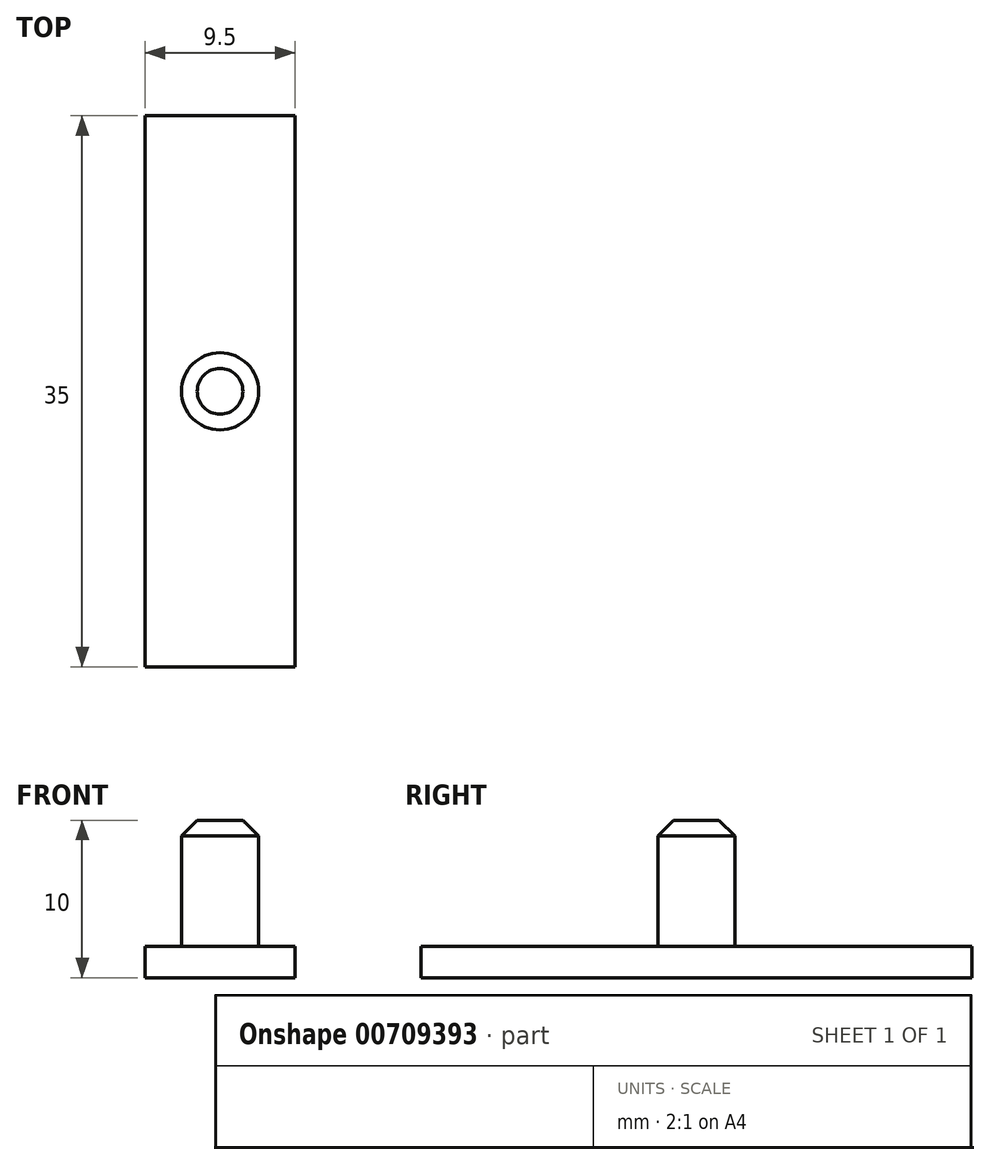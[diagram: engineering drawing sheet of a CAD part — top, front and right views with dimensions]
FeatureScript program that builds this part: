
annotation { "Feature Type Name" : "Feature", "Feature Type Description" : "" }
export const myFeature = defineFeature(function(context is Context, id is Id, definition is map)
    precondition{}
    {
        {
            var Q0;
            Q0=qCreatedBy(makeId("Top.planeOp"),FACE);
            var sketch = newSketch(context, id + "F0", { "sketchPlane" : qUnion([Q0])});
            skLineSegment(sketch, "E0.bottom", {"start": v(0, 0) * mm, "end": v(9.5, 0) * mm});
            skLineSegment(sketch, "E0.top", {"start": v(0, 35) * mm, "end": v(9.5, 35) * mm});
            skLineSegment(sketch, "E0.left", {"start": v(0, 0) * mm, "end": v(0, 35) * mm});
            skLineSegment(sketch, "E0.right", {"start": v(9.5, 0) * mm, "end": v(9.5, 35) * mm});
            skSolve(sketch);
        }
        {
            var Q0;
            Q0=makeQuery(id+"F0.imprint","IMPRINT",FACE,{"disambiguationData":[TD([[makeQuery(id+"F0.imprint","IMPRINT",EDGE,{"derivedFrom":sQuery(id+"F0.wireOp",EDGE,"E0.bottom")}),1.0]])]});
            extrude(context, id + "F1", {"entities" : qUnion([Q0]), "depth" : 2 * mm, "offsetDistance" : 25 * mm});
        }
        {
            var Q0;
            Q0=makeQuery(id+"F1.opExtrude","CAP_FACE",FACE,{"disambiguationData":[OSD([sQuery(id+"F0.wireOp",EDGE,"E0.bottom"),sQuery(id+"F0.wireOp",EDGE,"E0.top"),sQuery(id+"F0.wireOp",EDGE,"E0.left"),sQuery(id+"F0.wireOp",EDGE,"E0.right")])],"isStart":false});
            var sketch = newSketch(context, id + "F2", { "sketchPlane" : qUnion([Q0])});
            skLineSegment(sketch, "E1", {"start": v(0, 17.5) * mm, "end": v(4.75, 17.5) * mm, "construction": true});
            skLineSegment(sketch, "E2", {"start": v(4.75, 17.5) * mm, "end": v(4.75, 0) * mm, "construction": true});
            skCircle(sketch, "E3", {"center": v(4.75, 17.5) * mm, "radius": 2.45 * mm});
            skSolve(sketch);
        }
        {
            var Q0;
            Q0=makeQuery(id+"F2.imprint","IMPRINT",FACE,{"disambiguationData":[TD([[makeQuery(id+"F2.imprint","IMPRINT",EDGE,{"derivedFrom":sQuery(id+"F2.wireOp",EDGE,"E3")}),1.0]])]});
            extrude(context, id + "F3", {"entities" : qUnion([Q0]), "operationType" : NewBodyOperationType.ADD, "depth" : 8 * mm, "offsetDistance" : 25 * mm});
        }
        {
            var Q0;
            Q0=makeQuery(id+"F3.opExtrude","CAP_EDGE",EDGE,{"disambiguationData":[OSD([sQuery(id+"F2.wireOp",EDGE,"E3")])],"isStart":false});
            chamfer(context, id + "F4", {"entities" : qUnion([Q0]), "width" : 1 * mm, "tangentPropagation" : true});
        }
    });
